# Revit family: PRD_AR_WllHngWshbsns_EXOSSingleWashbasin_ANMW0010N1
name_source: partatom
category: Plumbing Fixtures
units: mm (PartAtom-declared; Revit-internal decimal feet)

## family parameters
Cut with Voids When Loaded = Yes
Enable Cutting in Views = No
Host = Face
Maintain Annotation Orientation = No
OmniClass Number = 23.45.05.14.14
OmniClass Title = Sinks/Lavatories
Part Type = Normal
Room Calculation Point = No
Round Connector Dimension = Use Diameter
Shared = No

## types (1)
- ANMW0010N
    AssetType = Fixed
    BIMObjectName = PRD_AR_WallHungWashbasins_EXOSSingleWashbasin_ANMW0010N
    BarrierFree = No
    BowlPosition = Center
    BowlShape = Rectangle
    Category = Pr_40_20_96_96, Wall-hung washbasins
    Color = Alpinewhite
    Default Elevation = 925 mm  [stored 3.03478 ft]
    Description = EXOS. single washbasin made of MIRANIT resin-bonded mineralmaterial with pore-free, smooth surface (temperature-resistant up to 80 °C), Alpine white colour. Roll-under, with storage areas, seamless moulded bowl, without overflow, with tap hole 35 mm (D). Mounting on washbasin back panel, including mounting material.
    DiameterNominal = 32  [stored 0.104987 ft]
    DrainSize = 32 mm  [stored 0.104987 ft]
    Export Type to IFC As = IfcSanitaryTerminalType
    Features = Alpine white colour. Roll-under, with storage areas, seamless moulded bowl, without overflow, with tap hole 35 mm (D).
    Flow = 0.0 L/s
    IfcExportAs = ifcSanitaryTerminalType
    IfcExportType = WASHHANDBASIN
    Manufacturer = KWC Group Management AG
    ManufacturerName = KWC Group Management AG
    ManufacturerURL = www.kwc-professional.com
    Material = Mineral Material
    MaterialCode = Miranit
    Model = ANMW0010N
    ModelNumber = 2030073251
    ModelReference = ANMW0010N
    Mounting = WALLHUNG
    MountingOffset = 0 mm  [stored 0 ft]
    NBSDescription = Wall hung wash basins
    NBSReference = 45-35-70/369
    Name = EXOS Single washbasin ANMW0010N
    NominalDepth = 500 mm  [stored 1.64042 ft]
    NominalHeight = 125 mm  [stored 0.410105 ft]
    NominalWidth = 600 mm
    NumberOfTapHoles = 1
    OverallDepth = 500 mm  [stored 1.64042 ft]
    OverallWidth = 600 mm
    Overflow = No
    ProductInformation = http://pim.kwc.com
    RearUpstand = No
    Shape = Rectangle
    SinkMaterial = PRD_AR_MineralMaterial_Alpinewhite
    SiphonIncluded = No
    Size = 32
    TapHole = Yes
    TapHoleDiameter = 35
    TapHolePosition = Middle
    TapLedge = Yes
    Type IFC Predefined Type = WASHHANDBASIN
    TypeOfBasin = Single
    TypeOfMounting = Wall Mounting
    URL = www.kwc-professional.com
    Uniclass2015Code = Pr_40_20_96_96
    Uniclass2015Title = Wall-hung washbasins
    Uniclass2015Version = Products v1.36
    Version = 1
    WashHandBasinType = OTHER
    WasteHolePosition = Centre Back
    WasteKitIncluded = Yes
    WasteSize = DN 32
    WasteSleeveIncluded = No

note: [stored X ft] marks values corroborated as IEEE doubles in the binary element streams (Revit-internal decimal feet)

## geometry (parser evidence)
native form markers: Sweep x6
no freeform markers — native parametric forms only
